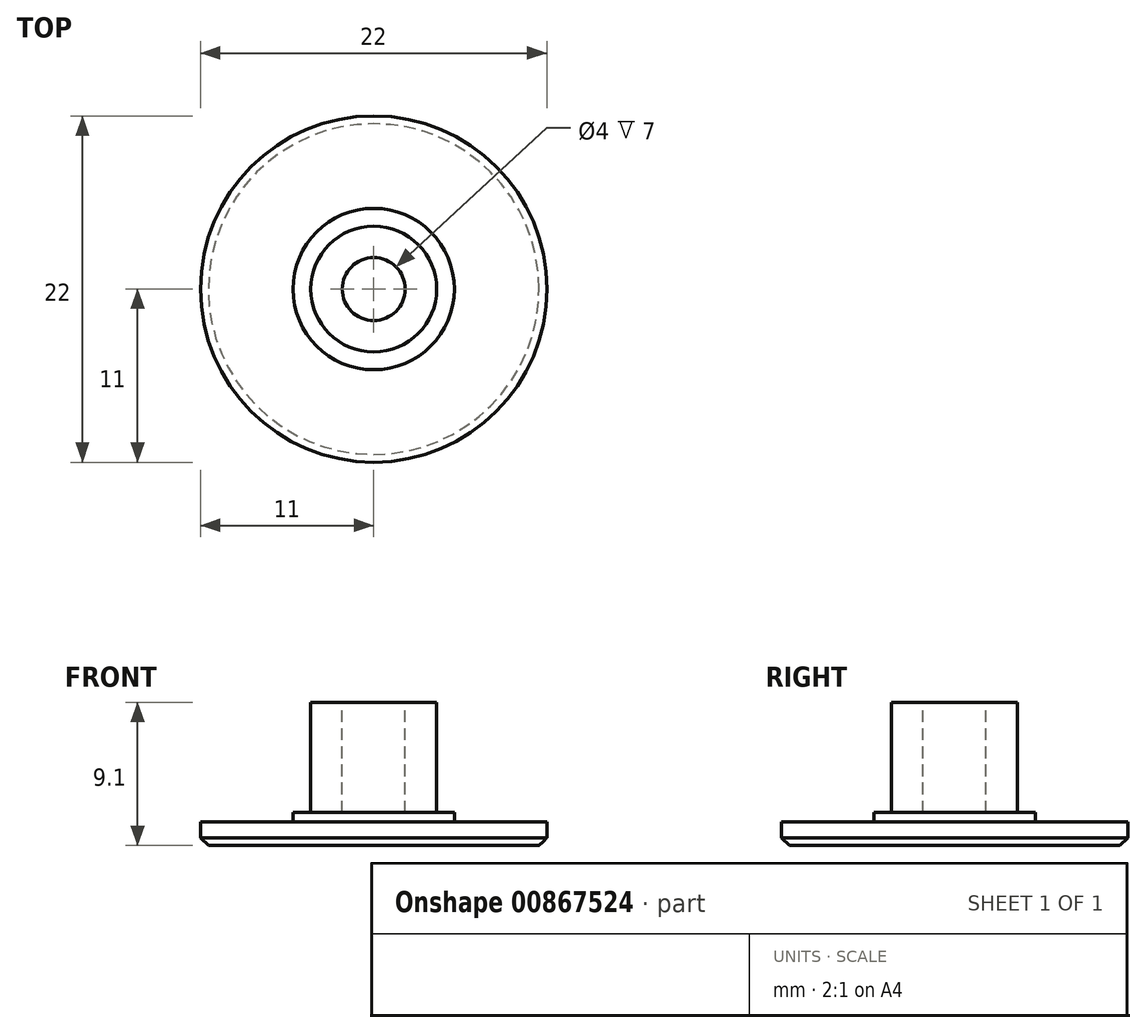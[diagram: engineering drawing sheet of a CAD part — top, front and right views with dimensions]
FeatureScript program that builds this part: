
annotation { "Feature Type Name" : "Feature", "Feature Type Description" : "" }
export const myFeature = defineFeature(function(context is Context, id is Id, definition is map)
    precondition{}
    {
        {
            var Q0;
            Q0=qCreatedBy(makeId("Top.planeOp"),FACE);
            var sketch = newSketch(context, id + "F0", { "sketchPlane" : qUnion([Q0])});
            skCircle(sketch, "E0", {"center": v(0, 0) * mm, "radius": 11 * mm});
            skSolve(sketch);
        }
        {
            var Q0;
            Q0=makeQuery(id+"F0.imprint","IMPRINT",FACE,{"disambiguationData":[TD([[makeQuery(id+"F0.imprint","IMPRINT",EDGE,{"derivedFrom":sQuery(id+"F0.wireOp",EDGE,"E0")}),1.0]])]});
            extrude(context, id + "F1", {"entities" : qUnion([Q0]), "depth" : 1.5 * mm, "offsetDistance" : 25 * mm});
        }
        {
            var Q0;
            Q0=makeQuery(id+"F1.opExtrude","CAP_FACE",FACE,{"disambiguationData":[OSD([sQuery(id+"F0.wireOp",EDGE,"E0")])],"isStart":false});
            var sketch = newSketch(context, id + "F2", { "sketchPlane" : qUnion([Q0])});
            skCircle(sketch, "E1", {"center": v(0, 0) * mm, "radius": 5.12 * mm});
            skSolve(sketch);
        }
        {
            var Q0;
            Q0=makeQuery(id+"F2.imprint","IMPRINT",FACE,{"disambiguationData":[TD([[makeQuery(id+"F2.imprint","IMPRINT",EDGE,{"derivedFrom":sQuery(id+"F2.wireOp",EDGE,"E1")}),1.0]])]});
            extrude(context, id + "F3", {"entities" : qUnion([Q0]), "operationType" : NewBodyOperationType.ADD, "depth" : .6 * mm, "offsetDistance" : 25 * mm});
        }
        {
            var Q0;
            Q0=makeQuery(id+"F3.opExtrude","CAP_FACE",FACE,{"disambiguationData":[OSD([sQuery(id+"F2.wireOp",EDGE,"E1")])],"isStart":false});
            var sketch = newSketch(context, id + "F4", { "sketchPlane" : qUnion([Q0])});
            skCircle(sketch, "E2", {"center": v(0, 0) * mm, "radius": 4 * mm});
            skSolve(sketch);
        }
        {
            var Q0;
            Q0 = qSketchRegion(id + "F4", true);
            extrude(context, id + "F5", {"entities" : qUnion([Q0]), "operationType" : NewBodyOperationType.ADD, "depth" : 7 * mm, "offsetDistance" : 25 * mm});
        }
        {
            var Q0;
            Q0=makeQuery(id+"F5.opExtrude","CAP_FACE",FACE,{"disambiguationData":[OSD([sQuery(id+"F4.wireOp",EDGE,"E2")])],"isStart":false});
            var sketch = newSketch(context, id + "F6", { "sketchPlane" : qUnion([Q0])});
            skCircle(sketch, "E3", {"center": v(0, 0) * mm, "radius": 2 * mm});
            skSolve(sketch);
        }
        {
            var Q0;
            Q0 = qSketchRegion(id + "F6", true);
            var Q1;
            Q1=makeQuery(id+"F3.opExtrude","CAP_FACE",FACE,{"disambiguationData":[OSD([sQuery(id+"F2.wireOp",EDGE,"E1")])],"isStart":false});
            extrude(context, id + "F7", {"entities" : qUnion([Q0]), "operationType" : NewBodyOperationType.REMOVE, "endBound" : BoundingType.UP_TO_SURFACE, "oppositeDirection" : true, "depth" : 25 * mm, "endBoundEntityFace" : qUnion([Q1]), "offsetDistance" : 25 * mm});
        }
        {
            var Q0;
            Q0=makeQuery(id+"F1.opExtrude","CAP_EDGE",EDGE,{"disambiguationData":[OSD([sQuery(id+"F0.wireOp",EDGE,"E0")])],"isStart":true});
            chamfer(context, id + "F8", {"entities" : qUnion([Q0]), "width" : .5 * mm, "tangentPropagation" : true});
        }
    });
